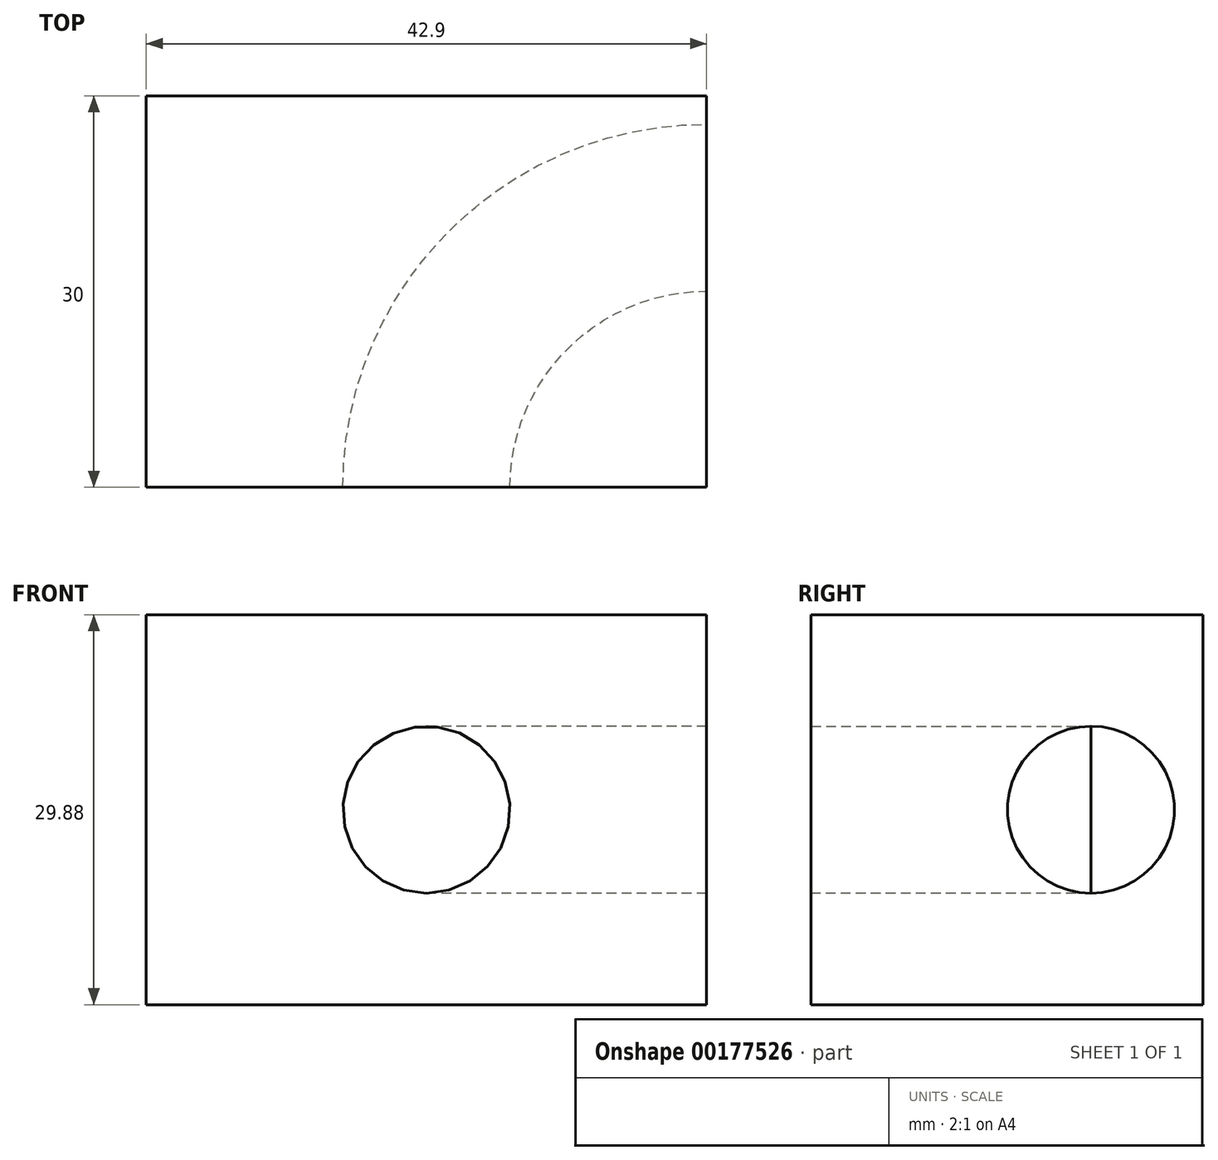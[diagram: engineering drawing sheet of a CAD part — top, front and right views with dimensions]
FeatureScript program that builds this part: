
annotation { "Feature Type Name" : "Feature", "Feature Type Description" : "" }
export const myFeature = defineFeature(function(context is Context, id is Id, definition is map)
    precondition{}
    {
        {
            var Q0;
            Q0=qCreatedBy(makeId("Front.planeOp"),FACE);
            var sketch = newSketch(context, id + "F0", { "sketchPlane" : qUnion([Q0])});
            skLineSegment(sketch, "E0.bottom", {"start": v(21.45, -14.94) * mm, "end": v(-21.45, -14.94) * mm});
            skLineSegment(sketch, "E0.top", {"start": v(21.45, 14.94) * mm, "end": v(-21.45, 14.94) * mm});
            skLineSegment(sketch, "E0.left", {"start": v(21.45, -14.94) * mm, "end": v(21.45, 14.94) * mm});
            skLineSegment(sketch, "E0.right", {"start": v(-21.45, -14.94) * mm, "end": v(-21.45, 14.94) * mm});
            skPoint(sketch, "E0.middle", {"position": v(0, 0) * mm});
            skSolve(sketch);
        }
        {
            var Q0;
            Q0=makeQuery(id+"F0.imprint","IMPRINT",FACE,{"disambiguationData":[TD([[makeQuery(id+"F0.imprint","IMPRINT",EDGE,{"derivedFrom":sQuery(id+"F0.wireOp",EDGE,"E0.bottom")}),-1.0]])]});
            extrude(context, id + "F1", {"entities" : qUnion([Q0]), "depth" : 30 * mm});
        }
        {
            var Q0;
            Q0=makeQuery(id+"F1.opExtrude","CAP_FACE",FACE,{"disambiguationData":[OSD([sQuery(id+"F0.wireOp",EDGE,"E0.bottom"),sQuery(id+"F0.wireOp",EDGE,"E0.top"),sQuery(id+"F0.wireOp",EDGE,"E0.left"),sQuery(id+"F0.wireOp",EDGE,"E0.right")])],"isStart":false});
            var sketch = newSketch(context, id + "F2", { "sketchPlane" : qUnion([Q0])});
            skCircle(sketch, "E1", {"center": v(0, 0) * mm, "radius": 6.4 * mm});
            skSolve(sketch);
        }
        {
            var Q0;
            Q0=qCreatedBy(makeId("Top.planeOp"),FACE);
            var sketch = newSketch(context, id + "F3", { "sketchPlane" : qUnion([Q0])});
            skArc(sketch, "E2", {"start": v(21.45, -8.58) * mm, "mid": v(6.28, -14.86) * mm, "end": v(0, -30.03) * mm});
            skSolve(sketch);
        }
        {
            var Q0;
            Q0=makeQuery(id+"F2.imprint","IMPRINT",FACE,{"disambiguationData":[TD([[makeQuery(id+"F2.imprint","IMPRINT",EDGE,{"derivedFrom":sQuery(id+"F2.wireOp",EDGE,"E1")}),1.0]])]});
            var Q1;
            Q1=sQuery(id+"F2.wireOp",EDGE,"E1");
            var Q2;
            Q2=sQuery(id+"F3.wireOp",EDGE,"E2");
            sweep(context, id + "F4", {"operationType" : NewBodyOperationType.REMOVE, "profiles" : qUnion([Q0]), "surfaceProfiles" : qUnion([Q1]), "path" : qUnion([Q2])});
        }
    });
